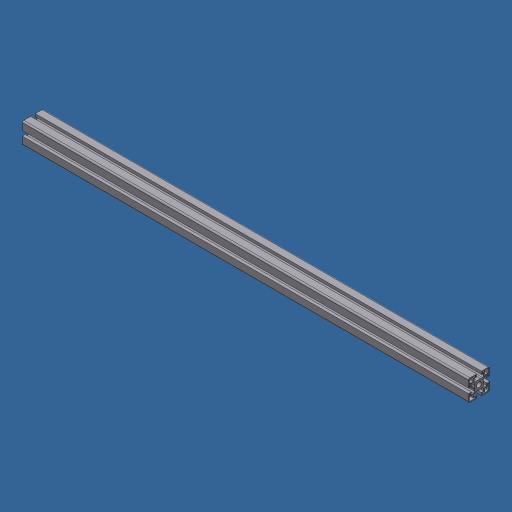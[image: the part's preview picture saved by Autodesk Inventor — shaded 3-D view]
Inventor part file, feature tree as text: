
AUTODESK INVENTOR PART (.ipt)
format: ipt  version: 2024.3 (Build 283343000, 343)  size: 235,008 bytes
history: native  units: mm (DEFAULTED — no unit token found)
features: other x1, plane x1, extrude x1, sketch x1
ambient origin geometry x8: Origin, YZ Plane, XZ Plane, XY Plane, X Axis, Y Axis, Z Axis, Center Point
bodies: Body1 (feature_tree)
feature tree (4):
  other  "Finish - None"
  plane  "Work Plane1"
  extrude  "BOSCH, 45X45"  Depth=945.0mm TaperAngle=0.0deg
  sketch  "Sketch1"  dims[d0=-188.9125mm d1=945.0mm d2=0.0mm]
